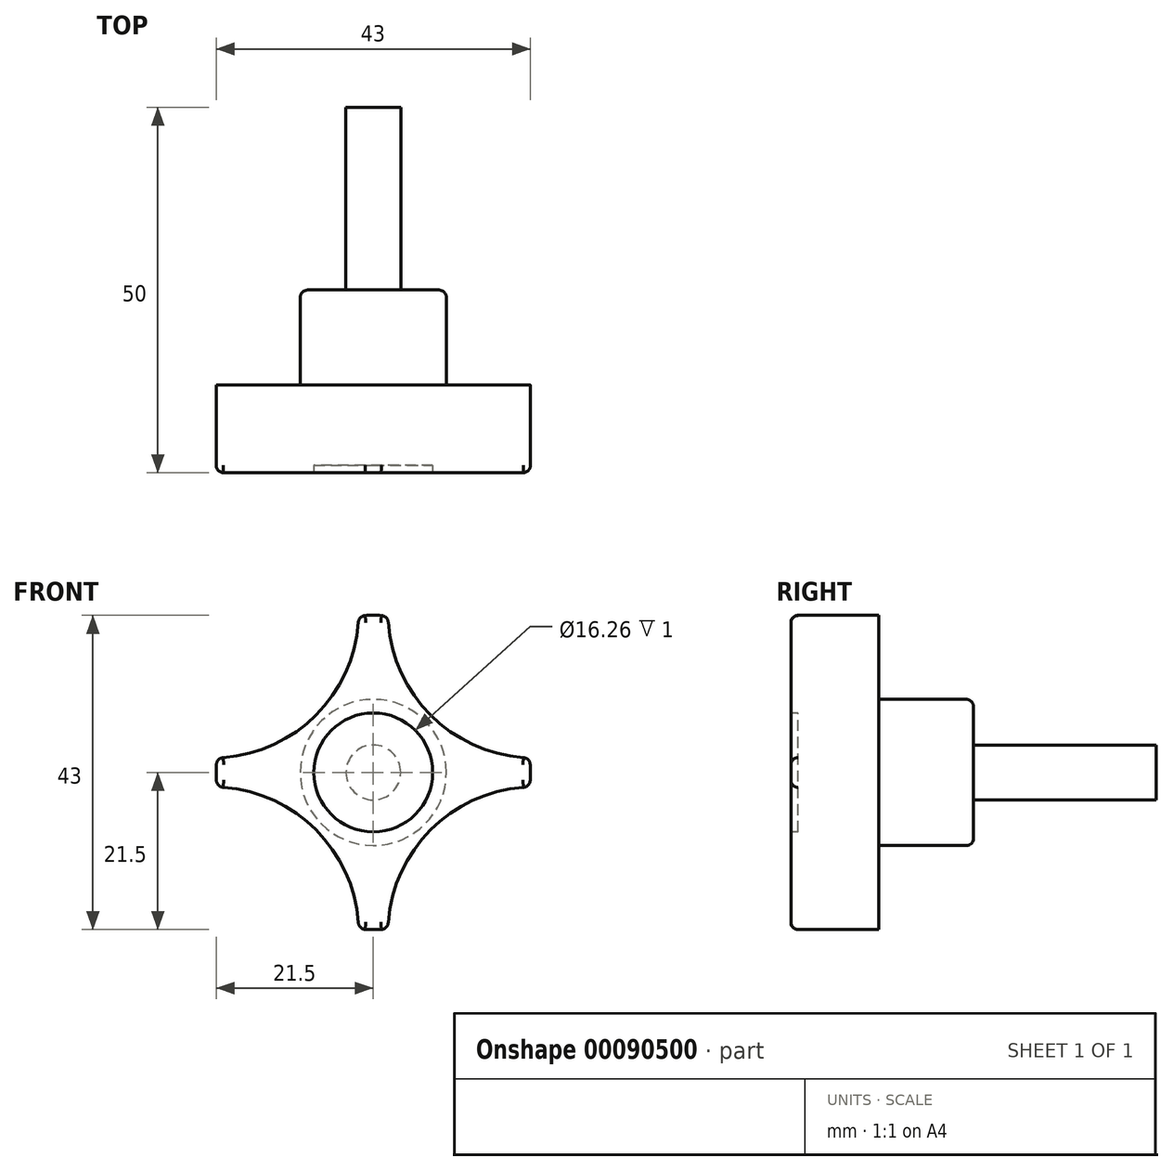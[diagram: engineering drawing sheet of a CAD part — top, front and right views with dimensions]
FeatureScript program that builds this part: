
annotation { "Feature Type Name" : "Feature", "Feature Type Description" : "" }
export const myFeature = defineFeature(function(context is Context, id is Id, definition is map)
    precondition{}
    {
        {
            var Q0;
            Q0=qCreatedBy(makeId("Front.planeOp"),FACE);
            var sketch = newSketch(context, id + "F0", { "sketchPlane" : qUnion([Q0])});
            skArc(sketch, "E0", {"start": v(-21.4, 2) * mm, "mid": v(-21.5, 0) * mm, "end": v(-21.4, -2) * mm});
            skArc(sketch, "E1", {"start": v(-21.4, 2) * mm, "mid": v(-7.85, 7.85) * mm, "end": v(-2, 21.4) * mm});
            skArc(sketch, "E2.MirrorCS", {"start": v(21.4, 2) * mm, "mid": v(7.85, 7.85) * mm, "end": v(2, 21.4) * mm});
            skArc(sketch, "E3.MirrorCS", {"start": v(21.4, -2) * mm, "mid": v(7.85, -7.85) * mm, "end": v(2, -21.4) * mm});
            skArc(sketch, "E4.MirrorCS", {"start": v(-21.4, -2) * mm, "mid": v(-7.85, -7.85) * mm, "end": v(-2, -21.4) * mm});
            skArc(sketch, "E5.trimOffspring", {"start": v(2, 21.4) * mm, "mid": v(0, 21.5) * mm, "end": v(-2, 21.4) * mm});
            skArc(sketch, "E6.trimOffspring", {"start": v(21.4, -2) * mm, "mid": v(21.5, 0) * mm, "end": v(21.4, 2) * mm});
            skArc(sketch, "E7.trimOffspring", {"start": v(-2, -21.4) * mm, "mid": v(0, -21.5) * mm, "end": v(2, -21.4) * mm});
            skSolve(sketch);
        }
        {
            var Q0;
            Q0=makeQuery(id+"F0.imprint","IMPRINT",FACE,{"disambiguationData":[TD([[makeQuery(id+"F0.imprint","IMPRINT",EDGE,{"derivedFrom":sQuery(id+"F0.wireOp",EDGE,"E0")}),1.0]])]});
            extrude(context, id + "F1", {"entities" : qUnion([Q0]), "endBound" : BoundingType.SYMMETRIC, "depth" : 12 * mm});
        }
        {
            var Q0;
            Q0=makeQuery(id+"F1.opExtrude","CAP_FACE",FACE,{"disambiguationData":[OSD([sQuery(id+"F0.wireOp",EDGE,"E0"),sQuery(id+"F0.wireOp",EDGE,"E1"),sQuery(id+"F0.wireOp",EDGE,"E2.MirrorCS"),sQuery(id+"F0.wireOp",EDGE,"E3.MirrorCS"),sQuery(id+"F0.wireOp",EDGE,"E4.MirrorCS"),sQuery(id+"F0.wireOp",EDGE,"E5.trimOffspring"),sQuery(id+"F0.wireOp",EDGE,"E6.trimOffspring"),sQuery(id+"F0.wireOp",EDGE,"E7.trimOffspring")])],"isStart":false});
            var sketch = newSketch(context, id + "F2", { "sketchPlane" : qUnion([Q0])});
            skCircle(sketch, "E8", {"center": v(0, 0) * mm, "radius": 8.13 * mm});
            skSolve(sketch);
        }
        {
            var Q0;
            Q0=makeQuery(id+"F2.imprint","IMPRINT",FACE,{"disambiguationData":[TD([[makeQuery(id+"F2.imprint","IMPRINT",EDGE,{"derivedFrom":sQuery(id+"F2.wireOp",EDGE,"E8")}),1.0]])]});
            extrude(context, id + "F3", {"entities" : qUnion([Q0]), "operationType" : NewBodyOperationType.REMOVE, "oppositeDirection" : true, "depth" : 1 * mm});
        }
        {
            var Q0;
            Q0=makeQuery(id+"F1.opExtrude","CAP_FACE",FACE,{"disambiguationData":[OSD([sQuery(id+"F0.wireOp",EDGE,"E0"),sQuery(id+"F0.wireOp",EDGE,"E1"),sQuery(id+"F0.wireOp",EDGE,"E2.MirrorCS"),sQuery(id+"F0.wireOp",EDGE,"E3.MirrorCS"),sQuery(id+"F0.wireOp",EDGE,"E4.MirrorCS"),sQuery(id+"F0.wireOp",EDGE,"E5.trimOffspring"),sQuery(id+"F0.wireOp",EDGE,"E6.trimOffspring"),sQuery(id+"F0.wireOp",EDGE,"E7.trimOffspring")])],"isStart":true});
            var sketch = newSketch(context, id + "F4", { "sketchPlane" : qUnion([Q0])});
            skCircle(sketch, "E9", {"center": v(0, 0) * mm, "radius": 10 * mm});
            skSolve(sketch);
        }
        {
            var Q0;
            Q0=makeQuery(id+"F4.imprint","IMPRINT",FACE,{"disambiguationData":[TD([[makeQuery(id+"F4.imprint","IMPRINT",EDGE,{"derivedFrom":sQuery(id+"F4.wireOp",EDGE,"E9")}),1.0]])]});
            extrude(context, id + "F5", {"entities" : qUnion([Q0]), "operationType" : NewBodyOperationType.ADD, "depth" : 13 * mm});
        }
        {
            var Q0;
            Q0=makeQuery(id+"F5.opExtrude","CAP_FACE",FACE,{"disambiguationData":[OSD([sQuery(id+"F4.wireOp",EDGE,"E9")])],"isStart":false});
            var sketch = newSketch(context, id + "F6", { "sketchPlane" : qUnion([Q0])});
            skCircle(sketch, "E10", {"center": v(0, 0) * mm, "radius": 3.75 * mm});
            skSolve(sketch);
        }
        {
            var Q0;
            Q0=makeQuery(id+"F6.imprint","IMPRINT",FACE,{"disambiguationData":[TD([[makeQuery(id+"F6.imprint","IMPRINT",EDGE,{"derivedFrom":sQuery(id+"F6.wireOp",EDGE,"E10")}),1.0]])]});
            extrude(context, id + "F7", {"entities" : qUnion([Q0]), "operationType" : NewBodyOperationType.ADD, "depth" : 25 * mm});
        }
        {
            var Q0;
            Q0=makeQuery(id+"F5.opExtrude","CAP_EDGE",EDGE,{"disambiguationData":[OSD([sQuery(id+"F4.wireOp",EDGE,"E9")])],"isStart":false});
            fillet(context, id + "F8", {"entities" : qUnion([Q0]), "radius" : 1 * mm, "tangentPropagation" : true, "allowEdgeOverflow" : false});
        }
        {
            var Q0;
            Q0=makeQuery(id+"F1.opExtrude","CAP_EDGE",EDGE,{"disambiguationData":[OSD([sQuery(id+"F0.wireOp",EDGE,"E2.MirrorCS")])],"isStart":false});
            var Q1;
            Q1=makeQuery(id+"F1.opExtrude","CAP_EDGE",EDGE,{"disambiguationData":[OSD([sQuery(id+"F0.wireOp",EDGE,"E5.trimOffspring")])],"isStart":false});
            var Q2;
            Q2=makeQuery(id+"F1.opExtrude","CAP_EDGE",EDGE,{"disambiguationData":[OSD([sQuery(id+"F0.wireOp",EDGE,"E1")])],"isStart":false});
            var Q3;
            Q3=makeQuery(id+"F1.opExtrude","CAP_EDGE",EDGE,{"disambiguationData":[OSD([sQuery(id+"F0.wireOp",EDGE,"E0")])],"isStart":false});
            var Q4;
            Q4=makeQuery(id+"F1.opExtrude","CAP_EDGE",EDGE,{"disambiguationData":[OSD([sQuery(id+"F0.wireOp",EDGE,"E4.MirrorCS")])],"isStart":false});
            var Q5;
            Q5=makeQuery(id+"F1.opExtrude","CAP_EDGE",EDGE,{"disambiguationData":[OSD([sQuery(id+"F0.wireOp",EDGE,"E7.trimOffspring")])],"isStart":false});
            var Q6;
            Q6=makeQuery(id+"F1.opExtrude","CAP_EDGE",EDGE,{"disambiguationData":[OSD([sQuery(id+"F0.wireOp",EDGE,"E3.MirrorCS")])],"isStart":false});
            var Q7;
            Q7=makeQuery(id+"F1.opExtrude","CAP_EDGE",EDGE,{"disambiguationData":[OSD([sQuery(id+"F0.wireOp",EDGE,"E6.trimOffspring")])],"isStart":false});
            fillet(context, id + "F9", {"entities" : qUnion([Q0, Q1, Q2, Q3, Q4, Q5, Q6, Q7]), "radius" : 1 * mm, "tangentPropagation" : true, "allowEdgeOverflow" : false});
        }
        {
            var Q0;
            Q0=makeQuery(id+"F1.opExtrude","SWEPT_EDGE",EDGE,{"disambiguationData":[OSD([sQuery(id+"F0.wireOp",EDGE,"E2.MirrorCS"),sQuery(id+"F0.wireOp",EDGE,"E6.trimOffspring")])]});
            var Q1;
            Q1=makeQuery(id+"F1.opExtrude","SWEPT_EDGE",EDGE,{"disambiguationData":[OSD([sQuery(id+"F0.wireOp",EDGE,"E3.MirrorCS"),sQuery(id+"F0.wireOp",EDGE,"E6.trimOffspring")])]});
            var Q2;
            Q2=makeQuery(id+"F1.opExtrude","SWEPT_EDGE",EDGE,{"disambiguationData":[OSD([sQuery(id+"F0.wireOp",EDGE,"E2.MirrorCS"),sQuery(id+"F0.wireOp",EDGE,"E5.trimOffspring")])]});
            var Q3;
            Q3=makeQuery(id+"F1.opExtrude","SWEPT_EDGE",EDGE,{"disambiguationData":[OSD([sQuery(id+"F0.wireOp",EDGE,"E1"),sQuery(id+"F0.wireOp",EDGE,"E5.trimOffspring")])]});
            var Q4;
            Q4=makeQuery(id+"F1.opExtrude","SWEPT_EDGE",EDGE,{"disambiguationData":[OSD([sQuery(id+"F0.wireOp",EDGE,"E0"),sQuery(id+"F0.wireOp",EDGE,"E1")])]});
            var Q5;
            Q5=makeQuery(id+"F1.opExtrude","SWEPT_EDGE",EDGE,{"disambiguationData":[OSD([sQuery(id+"F0.wireOp",EDGE,"E0"),sQuery(id+"F0.wireOp",EDGE,"E4.MirrorCS")])]});
            var Q6;
            Q6=makeQuery(id+"F1.opExtrude","SWEPT_EDGE",EDGE,{"disambiguationData":[OSD([sQuery(id+"F0.wireOp",EDGE,"E4.MirrorCS"),sQuery(id+"F0.wireOp",EDGE,"E7.trimOffspring")])]});
            var Q7;
            Q7=makeQuery(id+"F1.opExtrude","SWEPT_EDGE",EDGE,{"disambiguationData":[OSD([sQuery(id+"F0.wireOp",EDGE,"E3.MirrorCS"),sQuery(id+"F0.wireOp",EDGE,"E7.trimOffspring")])]});
            fillet(context, id + "F10", {"entities" : qUnion([Q0, Q1, Q2, Q3, Q4, Q5, Q6, Q7]), "radius" : 1 * mm, "tangentPropagation" : true, "allowEdgeOverflow" : false});
        }
    });
